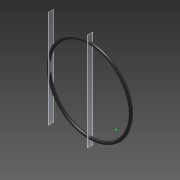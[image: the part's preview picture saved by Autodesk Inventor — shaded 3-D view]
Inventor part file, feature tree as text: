
AUTODESK INVENTOR PART (.ipt)
format: ipt  version: 2015 (Build 190159000, 159)  size: 146,944 bytes
history: native  units: mm
features: other x3, sketch x2, revolve x1, hole x1
ambient origin geometry x8: Origin, YZ Plane, XZ Plane, XY Plane, X Axis, Y Axis, Z Axis, Center Point
bodies: Body1 (feature_tree)
feature tree (7):
  other  "Bryła1"
  revolve  "Obrót1"
  other  "Płaszczyzna do otworu na wentyl 1"
  other  "Płaszczyzna do otworu na wentyl 1.1"
  hole  "Otwór na wentyl"  [1 undecoded]
  sketch  "Szkic1"
  sketch  "Szkic4"
note: 1 required parameter value undecoded (feature->parameter linkage not recoverable at this tier; creation-order binding heuristic only, values carry confidence <= 0.55)
